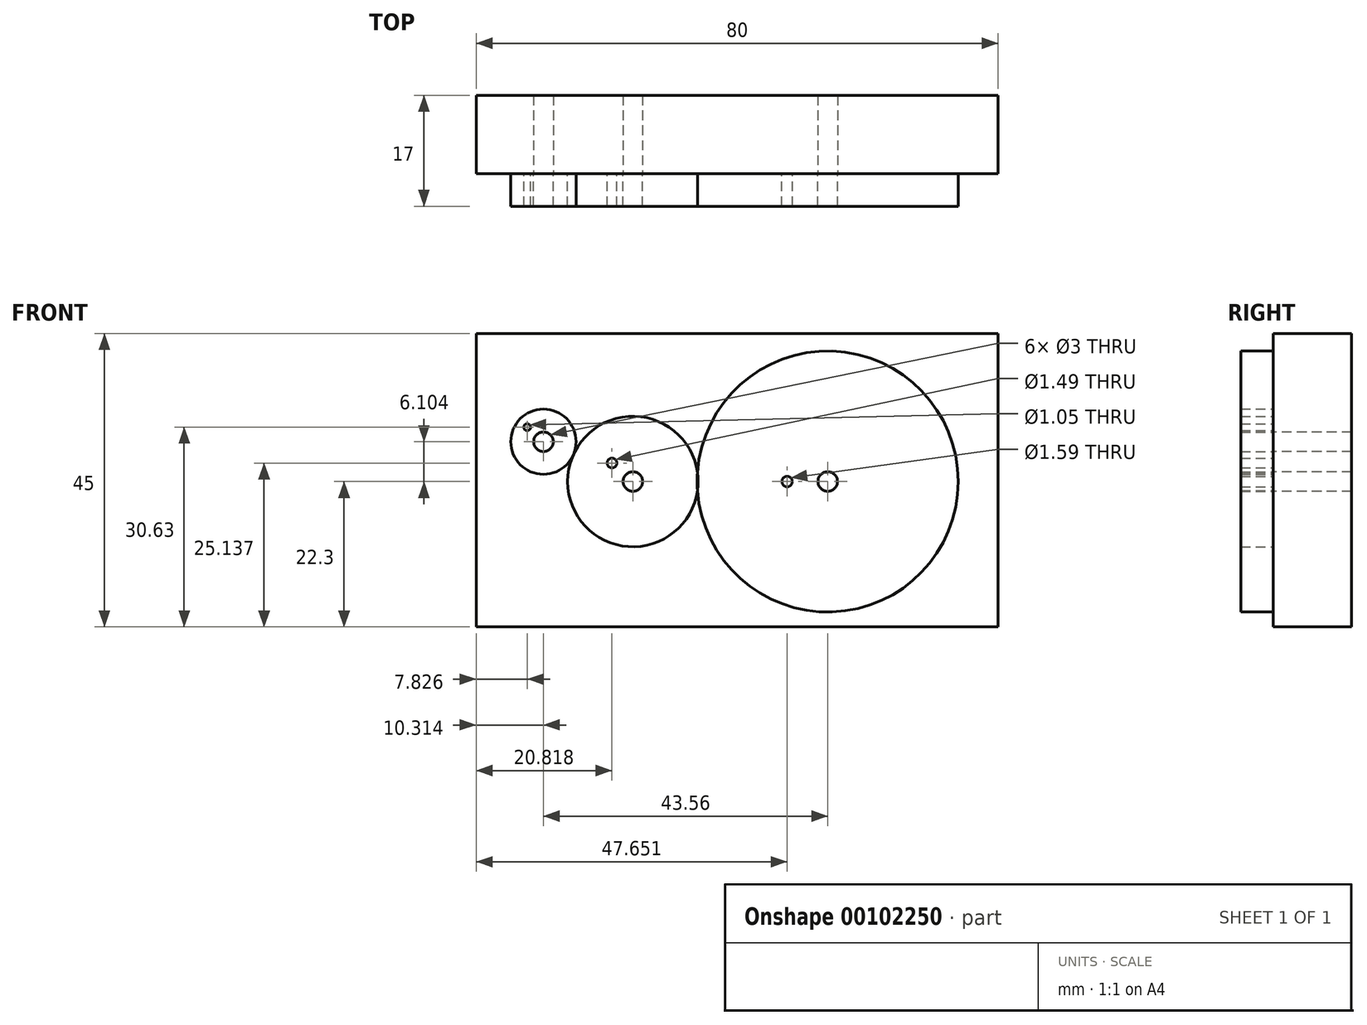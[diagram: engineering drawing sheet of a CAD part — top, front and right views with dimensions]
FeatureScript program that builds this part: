
annotation { "Feature Type Name" : "Feature", "Feature Type Description" : "" }
export const myFeature = defineFeature(function(context is Context, id is Id, definition is map)
    precondition{}
    {
        {
            var Q0;
            Q0=qCreatedBy(makeId("Front.planeOp"),FACE);
            var sketch = newSketch(context, id + "F0", { "sketchPlane" : qUnion([Q0])});
            skLineSegment(sketch, "E0.bottom", {"start": v(-40.16, 22.7) * mm, "end": v(39.84, 22.7) * mm});
            skLineSegment(sketch, "E0.top", {"start": v(-40.16, -22.3) * mm, "end": v(39.84, -22.3) * mm});
            skLineSegment(sketch, "E0.left", {"start": v(-40.16, 22.7) * mm, "end": v(-40.16, -22.3) * mm});
            skLineSegment(sketch, "E0.right", {"start": v(39.84, 22.7) * mm, "end": v(39.84, -22.3) * mm});
            skSolve(sketch);
        }
        {
            var Q0;
            Q0=makeQuery(id+"F0.imprint","IMPRINT",FACE,{"disambiguationData":[TD([[makeQuery(id+"F0.imprint","IMPRINT",EDGE,{"derivedFrom":sQuery(id+"F0.wireOp",EDGE,"E0.bottom")}),-1.0]])]});
            extrude(context, id + "F1", {"entities" : qUnion([Q0]), "depth" : 12 * mm});
        }
        {
            var Q0;
            Q0=makeQuery(id+"F1.opExtrude","CAP_FACE",FACE,{"disambiguationData":[OSD([sQuery(id+"F0.wireOp",EDGE,"E0.bottom"),sQuery(id+"F0.wireOp",EDGE,"E0.top"),sQuery(id+"F0.wireOp",EDGE,"E0.left"),sQuery(id+"F0.wireOp",EDGE,"E0.right")])],"isStart":false});
            var sketch = newSketch(context, id + "F2", { "sketchPlane" : qUnion([Q0])});
            skCircle(sketch, "E1", {"center": v(13.71, 0) * mm, "radius": 20 * mm});
            skCircle(sketch, "E2", {"center": v(-16.14, 0) * mm, "radius": 10 * mm});
            skCircle(sketch, "E3", {"center": v(-29.85, 6.1) * mm, "radius": 5 * mm});
            skCircle(sketch, "E4", {"center": v(13.71, 0) * mm, "radius": 1.5 * mm});
            skCircle(sketch, "E5", {"center": v(-16.14, 0) * mm, "radius": 1.5 * mm});
            skCircle(sketch, "E6", {"center": v(-29.85, 6.1) * mm, "radius": 1.5 * mm});
            skCircle(sketch, "E7", {"center": v(-32.33, 8.33) * mm, "radius": 0.53 * mm});
            skCircle(sketch, "E8", {"center": v(-19.34, 2.84) * mm, "radius": 0.74 * mm});
            skCircle(sketch, "E9", {"center": v(7.5, 0) * mm, "radius": 0.8 * mm});
            skSolve(sketch);
        }
        {
            var Q0;
            Q0=makeQuery(id+"F2.imprint","IMPRINT",FACE,{"disambiguationData":[TD([[makeQuery(id+"F2.imprint","IMPRINT",EDGE,{"derivedFrom":sQuery(id+"F2.wireOp",EDGE,"E4")}),-1.0]])]});
            var Q1;
            Q1=makeQuery(id+"F2.imprint","IMPRINT",FACE,{"disambiguationData":[TD([[makeQuery(id+"F2.imprint","IMPRINT",EDGE,{"derivedFrom":sQuery(id+"F2.wireOp",EDGE,"E5")}),-1.0]])]});
            var Q2;
            Q2=makeQuery(id+"F2.imprint","IMPRINT",FACE,{"disambiguationData":[TD([[makeQuery(id+"F2.imprint","IMPRINT",EDGE,{"derivedFrom":sQuery(id+"F2.wireOp",EDGE,"E3")}),1.0]])]});
            extrude(context, id + "F3", {"entities" : qUnion([Q0, Q1, Q2]), "depth" : 5 * mm});
        }
        {
            var Q0;
            Q0=sQuery(id+"F2.wireOp",VERTEX,"E1.center");
            var Q1;
            Q1=makeQuery(id+"F1.opExtrude","SWEPT_BODY",BODY,{"disambiguationData":[OSD([sQuery(id+"F0.wireOp",EDGE,"E0.bottom"),sQuery(id+"F0.wireOp",EDGE,"E0.top"),sQuery(id+"F0.wireOp",EDGE,"E0.left"),sQuery(id+"F0.wireOp",EDGE,"E0.right")])]});
            hole(context, id + "F4", {"style" : HoleStyle.SIMPLE, "endStyle" : HoleEndStyle.THROUGH, "holeDiameter" : 3 * mm, "majorDiameter" : 6.35 * mm, "locations" : qUnion([Q0]), "scope" : qUnion([Q1]), "isTappedThrough" : true, "tappedDepth" : 12.7 * mm, "tapClearance" : 3});
        }
        {
            var Q0;
            Q0=sQuery(id+"F2.wireOp",VERTEX,"E5.center");
            var Q1;
            Q1=makeQuery(id+"F1.opExtrude","SWEPT_BODY",BODY,{"disambiguationData":[OSD([sQuery(id+"F0.wireOp",EDGE,"E0.bottom"),sQuery(id+"F0.wireOp",EDGE,"E0.top"),sQuery(id+"F0.wireOp",EDGE,"E0.left"),sQuery(id+"F0.wireOp",EDGE,"E0.right")])]});
            hole(context, id + "F5", {"style" : HoleStyle.SIMPLE, "endStyle" : HoleEndStyle.THROUGH, "holeDiameter" : 3 * mm, "locations" : qUnion([Q0]), "scope" : qUnion([Q1]), "isTappedThrough" : true});
        }
        {
            var Q0;
            Q0=sQuery(id+"F2.wireOp",VERTEX,"E6.center");
            var Q1;
            Q1=makeQuery(id+"F1.opExtrude","SWEPT_BODY",BODY,{"disambiguationData":[OSD([sQuery(id+"F0.wireOp",EDGE,"E0.bottom"),sQuery(id+"F0.wireOp",EDGE,"E0.top"),sQuery(id+"F0.wireOp",EDGE,"E0.left"),sQuery(id+"F0.wireOp",EDGE,"E0.right")])]});
            hole(context, id + "F6", {"style" : HoleStyle.SIMPLE, "endStyle" : HoleEndStyle.THROUGH, "holeDiameter" : 3 * mm, "locations" : qUnion([Q0]), "scope" : qUnion([Q1]), "isTappedThrough" : true});
        }
    });
